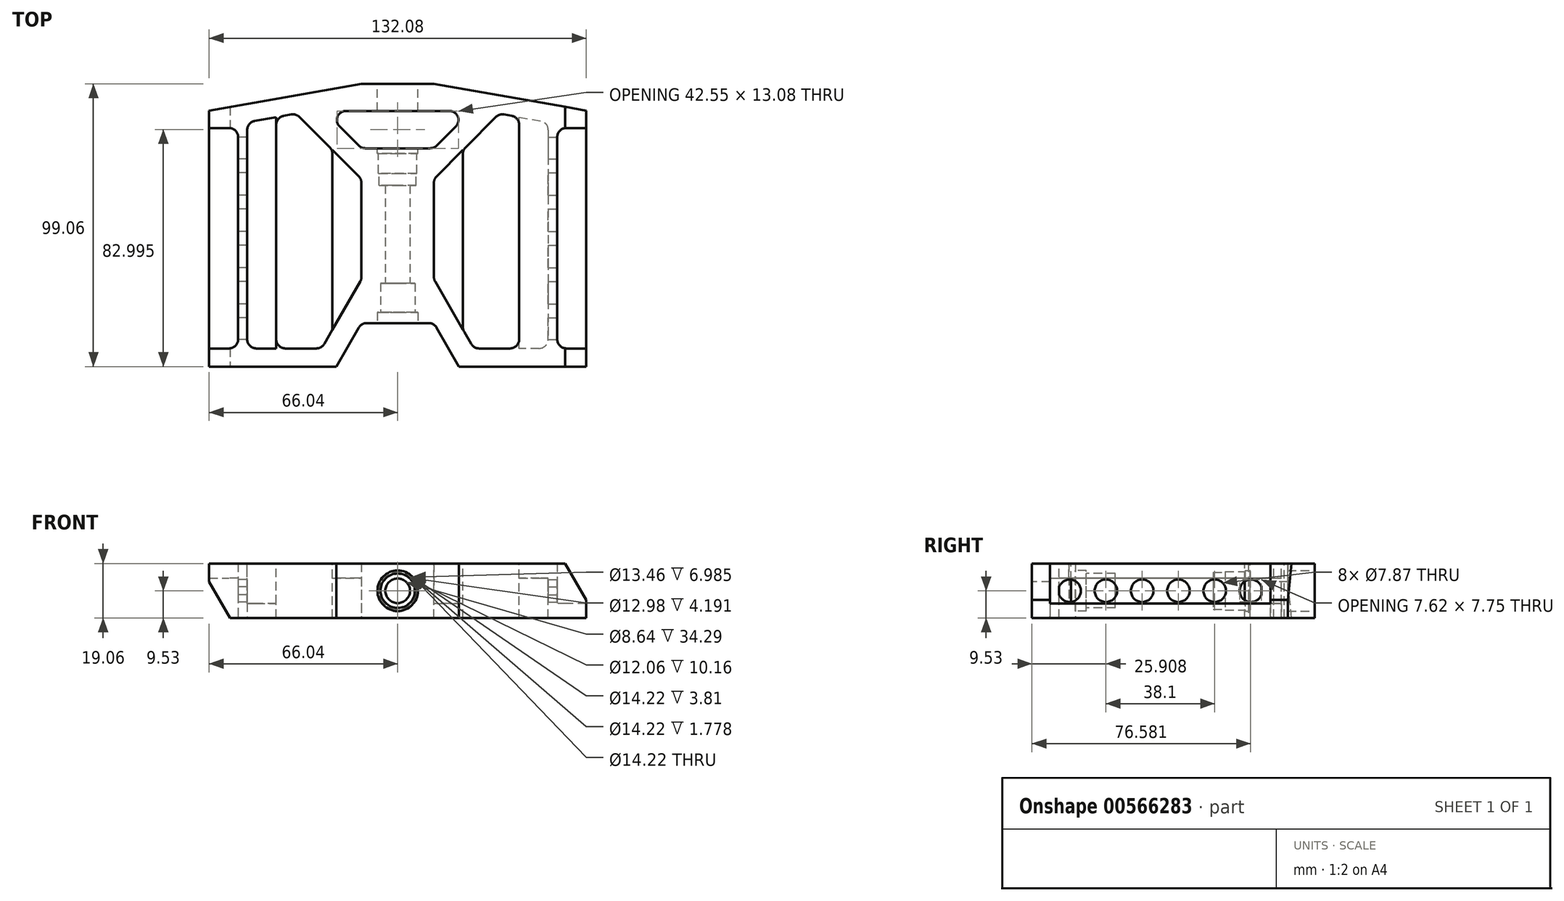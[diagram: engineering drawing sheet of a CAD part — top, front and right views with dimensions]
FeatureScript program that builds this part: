
annotation { "Feature Type Name" : "Feature", "Feature Type Description" : "" }
export const myFeature = defineFeature(function(context is Context, id is Id, definition is map)
    precondition{}
    {
        {
            var Q0;
            Q0=qCreatedBy(makeId("Top.planeOp"),FACE);
            var sketch = newSketch(context, id + "F0", { "sketchPlane" : qUnion([Q0])});
            skLineSegment(sketch, "E0", {"start": v(66.04, 89.53) * mm, "end": v(47.92, 89.53) * mm});
            skLineSegment(sketch, "E1", {"start": v(45.68, 84.11) * mm, "end": v(52.41, 77.38) * mm});
            skLineSegment(sketch, "E2", {"start": v(54.66, 76.45) * mm, "end": v(66.04, 76.45) * mm});
            skLineSegment(sketch, "E3", {"start": v(66.04, 76.45) * mm, "end": v(66.04, 89.53) * mm});
            skPoint(sketch, "E4.visualSharp", {"position": v(40.26, 89.53) * mm});
            skArc(sketch, "E4.filletArc", {"start": v(47.92, 89.53) * mm, "mid": v(45, 87.58) * mm, "end": v(45.68, 84.11) * mm});
            skPoint(sketch, "E5.visualSharp", {"position": v(53.34, 76.45) * mm});
            skArc(sketch, "E5.filletArc", {"start": v(52.41, 77.38) * mm, "mid": v(53.44, 76.7) * mm, "end": v(54.66, 76.45) * mm});
            skSolve(sketch);
        }
        {
            var Q0;
            Q0=qCreatedBy(makeId("Top.planeOp"),FACE);
            var sketch = newSketch(context, id + "F1", { "sketchPlane" : qUnion([Q0])});
            skLineSegment(sketch, "E6", {"start": v(0, 0) * mm, "end": v(0, 89.65) * mm});
            skLineSegment(sketch, "E7", {"start": v(0, 89.65) * mm, "end": v(53.34, 99.06) * mm});
            skLineSegment(sketch, "E8", {"start": v(53.34, 99.06) * mm, "end": v(66.04, 99.06) * mm});
            skLineSegment(sketch, "E9", {"start": v(66.04, 99.06) * mm, "end": v(66.04, 15.24) * mm});
            skLineSegment(sketch, "E10", {"start": v(66.04, 15.24) * mm, "end": v(55.17, 15.24) * mm});
            skLineSegment(sketch, "E11", {"start": v(52.42, 13.65) * mm, "end": v(44.54, 0) * mm});
            skLineSegment(sketch, "E12", {"start": v(44.54, 0) * mm, "end": v(0, 0) * mm});
            skPoint(sketch, "E13.visualSharp", {"position": v(53.34, 15.24) * mm});
            skArc(sketch, "E13.filletArc", {"start": v(55.17, 15.24) * mm, "mid": v(53.59, 14.81) * mm, "end": v(52.42, 13.65) * mm});
            skSolve(sketch);
        }
        {
            var Q0;
            Q0=makeQuery(id+"F1.imprint","IMPRINT",FACE,{"disambiguationData":[TD([[makeQuery(id+"F1.imprint","IMPRINT",EDGE,{"derivedFrom":sQuery(id+"F1.wireOp",EDGE,"E6")}),-1.0]])]});
            var sketch = newSketch(context, id + "F2", { "sketchPlane" : qUnion([Q0])});
            skLineSegment(sketch, "E14", {"start": v(43.18, 75.84) * mm, "end": v(43.18, 12.88) * mm});
            skLineSegment(sketch, "E15", {"start": v(43.18, 12.88) * mm, "end": v(52.91, 29.74) * mm});
            skLineSegment(sketch, "E16", {"start": v(53.34, 31.33) * mm, "end": v(53.34, 64.36) * mm});
            skLineSegment(sketch, "E17", {"start": v(52.41, 66.6) * mm, "end": v(43.18, 75.84) * mm});
            skPoint(sketch, "E18.visualSharp", {"position": v(53.34, 65.68) * mm});
            skArc(sketch, "E18.filletArc", {"start": v(53.34, 64.36) * mm, "mid": v(53.1, 65.58) * mm, "end": v(52.41, 66.6) * mm});
            skPoint(sketch, "E19.visualSharp", {"position": v(53.34, 30.48) * mm});
            skArc(sketch, "E19.filletArc", {"start": v(52.91, 29.74) * mm, "mid": v(53.23, 30.5) * mm, "end": v(53.34, 31.33) * mm});
            skSolve(sketch);
        }
        {
            var Q0;
            Q0=makeQuery(id+"F1.imprint","IMPRINT",FACE,{"disambiguationData":[TD([[makeQuery(id+"F1.imprint","IMPRINT",EDGE,{"derivedFrom":sQuery(id+"F1.wireOp",EDGE,"E6")}),-1.0]])]});
            var sketch = newSketch(context, id + "F3", { "sketchPlane" : qUnion([Q0])});
            skLineSegment(sketch, "E20", {"start": v(42.25, 76.77) * mm, "end": v(31.61, 87.4) * mm});
            skLineSegment(sketch, "E21", {"start": v(28.82, 88.29) * mm, "end": v(26.12, 87.81) * mm});
            skLineSegment(sketch, "E22", {"start": v(23.5, 84.69) * mm, "end": v(23.5, 9.52) * mm});
            skLineSegment(sketch, "E23", {"start": v(26.67, 6.35) * mm, "end": v(37.58, 6.35) * mm});
            skLineSegment(sketch, "E24", {"start": v(40.33, 7.94) * mm, "end": v(43.18, 12.88) * mm});
            skLineSegment(sketch, "E25", {"start": v(43.18, 12.88) * mm, "end": v(43.18, 74.52) * mm});
            skPoint(sketch, "E26.visualSharp", {"position": v(30.44, 88.57) * mm});
            skArc(sketch, "E26.filletArc", {"start": v(31.61, 87.4) * mm, "mid": v(30.32, 88.19) * mm, "end": v(28.82, 88.29) * mm});
            skPoint(sketch, "E27.visualSharp", {"position": v(23.5, 87.35) * mm});
            skArc(sketch, "E27.filletArc", {"start": v(26.12, 87.81) * mm, "mid": v(24.24, 86.73) * mm, "end": v(23.5, 84.69) * mm});
            skPoint(sketch, "E28.visualSharp", {"position": v(23.5, 6.35) * mm});
            skArc(sketch, "E28.filletArc", {"start": v(23.5, 9.52) * mm, "mid": v(24.42, 7.28) * mm, "end": v(26.67, 6.35) * mm});
            skPoint(sketch, "E29.visualSharp", {"position": v(39.4, 6.35) * mm});
            skArc(sketch, "E29.filletArc", {"start": v(37.58, 6.35) * mm, "mid": v(39.16, 6.78) * mm, "end": v(40.33, 7.94) * mm});
            skPoint(sketch, "E30.visualSharp", {"position": v(43.18, 75.84) * mm});
            skArc(sketch, "E30.filletArc", {"start": v(43.18, 74.52) * mm, "mid": v(42.94, 75.74) * mm, "end": v(42.25, 76.77) * mm});
            skCircle(sketch, "E31", {"center": v(40, 13.73) * mm, "radius": 3.18 * mm});
            skSolve(sketch);
        }
        {
            var Q0;
            Q0=makeQuery(id+"F1.imprint","IMPRINT",FACE,{"disambiguationData":[TD([[makeQuery(id+"F1.imprint","IMPRINT",EDGE,{"derivedFrom":sQuery(id+"F1.wireOp",EDGE,"E6")}),-1.0]])]});
            var sketch = newSketch(context, id + "F4", { "sketchPlane" : qUnion([Q0])});
            skLineSegment(sketch, "E32", {"start": v(23.5, 87.35) * mm, "end": v(15.96, 86.02) * mm});
            skLineSegment(sketch, "E33", {"start": v(13.33, 82.9) * mm, "end": v(13.33, 9.52) * mm});
            skLineSegment(sketch, "E34", {"start": v(16.5, 6.35) * mm, "end": v(23.5, 6.35) * mm});
            skLineSegment(sketch, "E35", {"start": v(23.5, 6.35) * mm, "end": v(23.5, 87.35) * mm});
            skPoint(sketch, "E36.visualSharp", {"position": v(13.33, 85.56) * mm});
            skArc(sketch, "E36.filletArc", {"start": v(15.96, 86.02) * mm, "mid": v(14.08, 84.93) * mm, "end": v(13.33, 82.9) * mm});
            skPoint(sketch, "E37.visualSharp", {"position": v(13.33, 6.35) * mm});
            skArc(sketch, "E37.filletArc", {"start": v(13.34, 9.52) * mm, "mid": v(14.26, 7.28) * mm, "end": v(16.5, 6.35) * mm});
            skLineSegment(sketch, "E38", {"start": v(23.5, 6.35) * mm, "end": v(26.7, 6.35) * mm});
            skLineSegment(sketch, "E39", {"start": v(23.5, 87.35) * mm, "end": v(26.43, 87.35) * mm});
            skSolve(sketch);
        }
        {
            var Q0;
            Q0=makeQuery(id+"F1.imprint","IMPRINT",FACE,{"disambiguationData":[TD([[makeQuery(id+"F1.imprint","IMPRINT",EDGE,{"derivedFrom":sQuery(id+"F1.wireOp",EDGE,"E6")}),-1.0]])]});
            var sketch = newSketch(context, id + "F5", { "sketchPlane" : qUnion([Q0])});
            skLineSegment(sketch, "E40", {"start": v(0, 83.57) * mm, "end": v(6.99, 83.57) * mm});
            skLineSegment(sketch, "E41", {"start": v(10.16, 80.4) * mm, "end": v(10.16, 9.52) * mm});
            skLineSegment(sketch, "E42", {"start": v(6.99, 6.35) * mm, "end": v(0, 6.35) * mm});
            skLineSegment(sketch, "E43", {"start": v(0, 6.35) * mm, "end": v(0, 83.57) * mm});
            skPoint(sketch, "E44.visualSharp", {"position": v(10.16, 83.57) * mm});
            skArc(sketch, "E44.filletArc", {"start": v(10.16, 80.4) * mm, "mid": v(9.23, 82.64) * mm, "end": v(6.99, 83.57) * mm});
            skPoint(sketch, "E45.visualSharp", {"position": v(10.16, 6.35) * mm});
            skArc(sketch, "E45.filletArc", {"start": v(6.99, 6.35) * mm, "mid": v(9.23, 7.28) * mm, "end": v(10.16, 9.52) * mm});
            skSolve(sketch);
        }
        {
            var Q0;
            Q0 = qSketchRegion(id + "F1", true);
            var Q1;
            Q1 = qSketchRegion(id + "F2", true);
            var Q2;
            Q2 = qSketchRegion(id + "F4", true);
            var Q3;
            Q3 = qSketchRegion(id + "F5", true);
            var Q4;
            Q4 = qSketchRegion(id + "F0", true);
            var Q5;
            Q5 = qSketchRegion(id + "F3", true);
            extrude(context, id + "F6", {"entities" : qUnion([Q0, Q1, Q2, Q3, Q4, Q5]), "endBound" : BoundingType.SYMMETRIC, "depth" : 19.05 * mm, "offsetDistance" : 25.4 * mm});
        }
        {
            var Q0;
            Q0=makeQuery(id+"F6.opExtrude","CAP_FACE",FACE,{"disambiguationData":[OSD([sQuery(id+"F0.wireOp",EDGE,"E0"),sQuery(id+"F0.wireOp",EDGE,"E1"),sQuery(id+"F0.wireOp",EDGE,"E2"),sQuery(id+"F0.wireOp",EDGE,"E3"),sQuery(id+"F0.wireOp",EDGE,"E4.filletArc"),sQuery(id+"F0.wireOp",EDGE,"E5.filletArc")])],"isStart":false});
            extrude(context, id + "F7", {"entities" : qUnion([Q0]), "operationType" : NewBodyOperationType.REMOVE, "endBound" : BoundingType.THROUGH_ALL, "oppositeDirection" : true, "depth" : 25.4 * mm, "offsetDistance" : 25.4 * mm});
        }
        {
            var Q0;
            Q0=makeQuery(id+"F6.opExtrude","CAP_FACE",FACE,{"disambiguationData":[OSD([sQuery(id+"F3.wireOp",EDGE,"E20"),sQuery(id+"F3.wireOp",EDGE,"E21"),sQuery(id+"F3.wireOp",EDGE,"E22"),sQuery(id+"F3.wireOp",EDGE,"E23"),sQuery(id+"F3.wireOp",EDGE,"E24"),sQuery(id+"F3.wireOp",EDGE,"E25"),sQuery(id+"F3.wireOp",EDGE,"E26.filletArc"),sQuery(id+"F3.wireOp",EDGE,"E27.filletArc"),sQuery(id+"F3.wireOp",EDGE,"E28.filletArc"),sQuery(id+"F3.wireOp",EDGE,"E29.filletArc"),sQuery(id+"F3.wireOp",EDGE,"E30.filletArc")])],"isStart":false});
            extrude(context, id + "F8", {"entities" : qUnion([Q0]), "operationType" : NewBodyOperationType.REMOVE, "endBound" : BoundingType.THROUGH_ALL, "oppositeDirection" : true, "depth" : 25.4 * mm, "offsetDistance" : 25.4 * mm});
        }
        {
            var Q0;
            Q0=makeQuery(id+"F6.opExtrude","CAP_FACE",FACE,{"disambiguationData":[OSD([sQuery(id+"F4.wireOp",EDGE,"E32"),sQuery(id+"F4.wireOp",EDGE,"E33"),sQuery(id+"F4.wireOp",EDGE,"E34"),sQuery(id+"F4.wireOp",EDGE,"E35"),sQuery(id+"F4.wireOp",EDGE,"E36.filletArc"),sQuery(id+"F4.wireOp",EDGE,"E37.filletArc")])],"isStart":false});
            extrude(context, id + "F9", {"entities" : qUnion([Q0]), "operationType" : NewBodyOperationType.REMOVE, "oppositeDirection" : true, "depth" : 13.97 * mm, "offsetDistance" : 25.4 * mm});
        }
        {
            var Q0;
            Q0=makeQuery(id+"F6.opExtrude","CAP_FACE",FACE,{"disambiguationData":[OSD([sQuery(id+"F5.wireOp",EDGE,"E40"),sQuery(id+"F5.wireOp",EDGE,"E41"),sQuery(id+"F5.wireOp",EDGE,"E42"),sQuery(id+"F5.wireOp",EDGE,"E43"),sQuery(id+"F5.wireOp",EDGE,"E44.filletArc"),sQuery(id+"F5.wireOp",EDGE,"E45.filletArc")])],"isStart":true});
            extrude(context, id + "F10", {"entities" : qUnion([Q0]), "operationType" : NewBodyOperationType.REMOVE, "oppositeDirection" : true, "depth" : 13.97 * mm, "offsetDistance" : 25.4 * mm});
        }
        {
            var Q0;
            Q0=makeQuery(id+"F6.opExtrude","CAP_FACE",FACE,{"disambiguationData":[OSD([sQuery(id+"F2.wireOp",EDGE,"E14"),sQuery(id+"F2.wireOp",EDGE,"E15"),sQuery(id+"F2.wireOp",EDGE,"E16"),sQuery(id+"F2.wireOp",EDGE,"E17"),sQuery(id+"F2.wireOp",EDGE,"E18.filletArc"),sQuery(id+"F2.wireOp",EDGE,"E19.filletArc")])],"isStart":true});
            extrude(context, id + "F11", {"entities" : qUnion([Q0]), "operationType" : NewBodyOperationType.REMOVE, "oppositeDirection" : true, "depth" : 13.97 * mm, "offsetDistance" : 25.4 * mm});
        }
        {
            var Q0;
            Q0=qCreatedBy(makeId("Top.planeOp"),FACE);
            var sketch = newSketch(context, id + "F12", { "sketchPlane" : qUnion([Q0])});
            skLineSegment(sketch, "E46", {"start": v(66.04, 15.24) * mm, "end": v(66.04, 99.06) * mm});
            skLineSegment(sketch, "E47", {"start": v(66.04, 99.06) * mm, "end": v(78.74, 99.06) * mm});
            skLineSegment(sketch, "E48", {"start": v(78.74, 99.06) * mm, "end": v(132.08, 89.65) * mm});
            skLineSegment(sketch, "E49", {"start": v(132.08, 89.65) * mm, "end": v(132.08, 0) * mm});
            skLineSegment(sketch, "E50", {"start": v(132.08, 0) * mm, "end": v(87.54, 0) * mm});
            skLineSegment(sketch, "E51", {"start": v(87.54, 0) * mm, "end": v(79.66, 13.65) * mm});
            skLineSegment(sketch, "E52", {"start": v(76.9, 15.24) * mm, "end": v(66.04, 15.24) * mm});
            skPoint(sketch, "E53.visualSharp", {"position": v(78.74, 15.24) * mm});
            skArc(sketch, "E53.filletArc", {"start": v(79.66, 13.65) * mm, "mid": v(78.5, 14.81) * mm, "end": v(76.9, 15.24) * mm});
            skSolve(sketch);
        }
        {
            var Q0;
            Q0=makeQuery(id+"F12.imprint","IMPRINT",FACE,{"disambiguationData":[TD([[makeQuery(id+"F12.imprint","IMPRINT",EDGE,{"derivedFrom":sQuery(id+"F12.wireOp",EDGE,"E46")}),-1.0]])]});
            var sketch = newSketch(context, id + "F13", { "sketchPlane" : qUnion([Q0])});
            skLineSegment(sketch, "E54", {"start": v(66.04, 89.53) * mm, "end": v(84.16, 89.53) * mm});
            skLineSegment(sketch, "E55", {"start": v(86.4, 84.11) * mm, "end": v(79.67, 77.38) * mm});
            skLineSegment(sketch, "E56", {"start": v(77.42, 76.45) * mm, "end": v(66.04, 76.45) * mm});
            skLineSegment(sketch, "E57", {"start": v(66.04, 76.45) * mm, "end": v(66.04, 89.53) * mm});
            skPoint(sketch, "E58.visualSharp", {"position": v(91.82, 89.53) * mm});
            skArc(sketch, "E58.filletArc", {"start": v(86.4, 84.11) * mm, "mid": v(87.09, 87.58) * mm, "end": v(84.16, 89.54) * mm});
            skPoint(sketch, "E59.visualSharp", {"position": v(78.74, 76.45) * mm});
            skArc(sketch, "E59.filletArc", {"start": v(77.42, 76.45) * mm, "mid": v(78.64, 76.7) * mm, "end": v(79.67, 77.38) * mm});
            skSolve(sketch);
        }
        {
            var Q0;
            Q0=makeQuery(id+"F12.imprint","IMPRINT",FACE,{"disambiguationData":[TD([[makeQuery(id+"F12.imprint","IMPRINT",EDGE,{"derivedFrom":sQuery(id+"F12.wireOp",EDGE,"E46")}),-1.0]])]});
            var sketch = newSketch(context, id + "F14", { "sketchPlane" : qUnion([Q0])});
            skLineSegment(sketch, "E60", {"start": v(88.9, 75.84) * mm, "end": v(88.9, 12.88) * mm});
            skLineSegment(sketch, "E61", {"start": v(88.9, 12.88) * mm, "end": v(79.17, 29.74) * mm});
            skLineSegment(sketch, "E62", {"start": v(78.74, 31.33) * mm, "end": v(78.74, 64.36) * mm});
            skLineSegment(sketch, "E63", {"start": v(79.67, 66.6) * mm, "end": v(88.9, 75.84) * mm});
            skPoint(sketch, "E64.visualSharp", {"position": v(78.74, 65.68) * mm});
            skArc(sketch, "E64.filletArc", {"start": v(79.67, 66.6) * mm, "mid": v(78.98, 65.58) * mm, "end": v(78.74, 64.36) * mm});
            skPoint(sketch, "E65.visualSharp", {"position": v(78.74, 30.48) * mm});
            skArc(sketch, "E65.filletArc", {"start": v(78.74, 31.33) * mm, "mid": v(78.85, 30.5) * mm, "end": v(79.17, 29.74) * mm});
            skSolve(sketch);
        }
        {
            var Q0;
            Q0=makeQuery(id+"F12.imprint","IMPRINT",FACE,{"disambiguationData":[TD([[makeQuery(id+"F12.imprint","IMPRINT",EDGE,{"derivedFrom":sQuery(id+"F12.wireOp",EDGE,"E46")}),-1.0]])]});
            var sketch = newSketch(context, id + "F15", { "sketchPlane" : qUnion([Q0])});
            skLineSegment(sketch, "E66", {"start": v(89.83, 76.77) * mm, "end": v(100.47, 87.4) * mm});
            skLineSegment(sketch, "E67", {"start": v(103.26, 88.29) * mm, "end": v(105.96, 87.81) * mm});
            skLineSegment(sketch, "E68", {"start": v(108.58, 84.69) * mm, "end": v(108.58, 9.53) * mm});
            skLineSegment(sketch, "E69", {"start": v(105.4, 6.35) * mm, "end": v(94.5, 6.35) * mm});
            skLineSegment(sketch, "E70", {"start": v(91.75, 7.94) * mm, "end": v(89.33, 12.15) * mm});
            skLineSegment(sketch, "E71", {"start": v(88.9, 13.73) * mm, "end": v(88.9, 74.52) * mm});
            skPoint(sketch, "E72.visualSharp", {"position": v(101.64, 88.57) * mm});
            skArc(sketch, "E72.filletArc", {"start": v(103.26, 88.29) * mm, "mid": v(101.76, 88.19) * mm, "end": v(100.47, 87.4) * mm});
            skPoint(sketch, "E73.visualSharp", {"position": v(108.59, 87.35) * mm});
            skArc(sketch, "E73.filletArc", {"start": v(108.59, 84.69) * mm, "mid": v(107.84, 86.73) * mm, "end": v(105.96, 87.81) * mm});
            skPoint(sketch, "E74.visualSharp", {"position": v(108.59, 6.35) * mm});
            skArc(sketch, "E74.filletArc", {"start": v(105.4, 6.35) * mm, "mid": v(107.66, 7.28) * mm, "end": v(108.59, 9.53) * mm});
            skPoint(sketch, "E75.visualSharp", {"position": v(92.67, 6.35) * mm});
            skArc(sketch, "E75.filletArc", {"start": v(91.75, 7.94) * mm, "mid": v(92.92, 6.78) * mm, "end": v(94.5, 6.35) * mm});
            skPoint(sketch, "E76.visualSharp", {"position": v(88.9, 75.84) * mm});
            skArc(sketch, "E76.filletArc", {"start": v(89.83, 76.77) * mm, "mid": v(89.14, 75.74) * mm, "end": v(88.9, 74.52) * mm});
            skPoint(sketch, "E77.visualSharp", {"position": v(88.9, 12.88) * mm});
            skArc(sketch, "E77.filletArc", {"start": v(88.9, 13.73) * mm, "mid": v(89, 12.91) * mm, "end": v(89.33, 12.15) * mm});
            skSolve(sketch);
        }
        {
            var Q0;
            Q0=makeQuery(id+"F12.imprint","IMPRINT",FACE,{"disambiguationData":[TD([[makeQuery(id+"F12.imprint","IMPRINT",EDGE,{"derivedFrom":sQuery(id+"F12.wireOp",EDGE,"E46")}),-1.0]])]});
            var sketch = newSketch(context, id + "F16", { "sketchPlane" : qUnion([Q0])});
            skLineSegment(sketch, "E78", {"start": v(108.59, 87.35) * mm, "end": v(116.12, 86.02) * mm});
            skLineSegment(sketch, "E79", {"start": v(118.75, 82.9) * mm, "end": v(118.75, 9.53) * mm});
            skLineSegment(sketch, "E80", {"start": v(115.57, 6.35) * mm, "end": v(108.59, 6.35) * mm});
            skLineSegment(sketch, "E81", {"start": v(108.59, 6.35) * mm, "end": v(108.59, 87.35) * mm});
            skPoint(sketch, "E82.visualSharp", {"position": v(118.75, 85.56) * mm});
            skArc(sketch, "E82.filletArc", {"start": v(118.75, 82.9) * mm, "mid": v(118, 84.93) * mm, "end": v(116.12, 86.02) * mm});
            skPoint(sketch, "E83.visualSharp", {"position": v(118.75, 6.35) * mm});
            skArc(sketch, "E83.filletArc", {"start": v(115.57, 6.35) * mm, "mid": v(117.82, 7.28) * mm, "end": v(118.75, 9.53) * mm});
            skSolve(sketch);
        }
        {
            var Q0;
            Q0=makeQuery(id+"F12.imprint","IMPRINT",FACE,{"disambiguationData":[TD([[makeQuery(id+"F12.imprint","IMPRINT",EDGE,{"derivedFrom":sQuery(id+"F12.wireOp",EDGE,"E46")}),-1.0]])]});
            var sketch = newSketch(context, id + "F17", { "sketchPlane" : qUnion([Q0])});
            skLineSegment(sketch, "E84", {"start": v(132.08, 83.57) * mm, "end": v(125.1, 83.57) * mm});
            skLineSegment(sketch, "E85", {"start": v(121.92, 80.4) * mm, "end": v(121.92, 9.53) * mm});
            skLineSegment(sketch, "E86", {"start": v(125.1, 6.35) * mm, "end": v(132.08, 6.35) * mm});
            skLineSegment(sketch, "E87", {"start": v(132.08, 6.35) * mm, "end": v(132.08, 83.57) * mm});
            skPoint(sketch, "E88.visualSharp", {"position": v(121.92, 83.57) * mm});
            skArc(sketch, "E88.filletArc", {"start": v(125.1, 83.57) * mm, "mid": v(122.85, 82.64) * mm, "end": v(121.92, 80.4) * mm});
            skPoint(sketch, "E89.visualSharp", {"position": v(121.92, 6.35) * mm});
            skArc(sketch, "E89.filletArc", {"start": v(121.92, 9.53) * mm, "mid": v(122.85, 7.28) * mm, "end": v(125.1, 6.35) * mm});
            skSolve(sketch);
        }
        {
            var Q0;
            Q0=makeQuery(id+"F12.imprint","IMPRINT",FACE,{"disambiguationData":[TD([[makeQuery(id+"F12.imprint","IMPRINT",EDGE,{"derivedFrom":sQuery(id+"F12.wireOp",EDGE,"E46")}),-1.0]])]});
            extrude(context, id + "F18", {"entities" : qUnion([Q0]), "operationType" : NewBodyOperationType.ADD, "endBound" : BoundingType.SYMMETRIC, "oppositeDirection" : true, "depth" : 19.05 * mm, "offsetDistance" : 25.4 * mm});
        }
        {
            var Q0;
            Q0 = qSketchRegion(id + "F13", true);
            extrude(context, id + "F19", {"entities" : qUnion([Q0]), "operationType" : NewBodyOperationType.REMOVE, "endBound" : BoundingType.SYMMETRIC, "depth" : 19.05 * mm, "offsetDistance" : 25.4 * mm});
        }
        {
            var Q0;
            Q0 = qSketchRegion(id + "F15", true);
            extrude(context, id + "F20", {"entities" : qUnion([Q0]), "operationType" : NewBodyOperationType.REMOVE, "endBound" : BoundingType.SYMMETRIC, "oppositeDirection" : true, "depth" : 19.05 * mm, "offsetDistance" : 25.4 * mm});
        }
        {
            var Q0;
            Q0 = qSketchRegion(id + "F14", true);
            extrude(context, id + "F21", {"entities" : qUnion([Q0]), "operationType" : NewBodyOperationType.REMOVE, "depth" : 9.52 * mm, "offsetDistance" : 25.4 * mm, "hasSecondDirection" : true, "secondDirectionOppositeDirection" : true, "secondDirectionDepth" : 4.44 * mm});
        }
        {
            var Q0;
            Q0 = qSketchRegion(id + "F16", true);
            extrude(context, id + "F22", {"entities" : qUnion([Q0]), "operationType" : NewBodyOperationType.REMOVE, "oppositeDirection" : true, "depth" : 9.52 * mm, "offsetDistance" : 25.4 * mm, "hasSecondDirection" : true, "secondDirectionOppositeDirection" : false, "secondDirectionDepth" : 4.44 * mm});
        }
        {
            var Q0;
            Q0 = qSketchRegion(id + "F17", true);
            extrude(context, id + "F23", {"entities" : qUnion([Q0]), "operationType" : NewBodyOperationType.REMOVE, "depth" : 9.52 * mm, "offsetDistance" : 25.4 * mm, "hasSecondDirection" : true, "secondDirectionOppositeDirection" : true, "secondDirectionDepth" : 4.44 * mm});
        }
        {
            var Q0;
            Q0=makeQuery(id+"F10.boolean.opBoolean","COPY",FACE,{"derivedFrom":makeQuery(id+"F10.opExtrude","SWEPT_FACE",FACE,{"disambiguationData":[OSD([sQuery(id+"F5.wireOp",EDGE,"E41")])]})});
            var sketch = newSketch(context, id + "F24", { "sketchPlane" : qUnion([Q0])});
            skCircle(sketch, "E90", {"center": v(-13.2, 0) * mm, "radius": 3.94 * mm});
            skCircle(sketch, "E91.1.0.0", {"center": v(-25.9, 0) * mm, "radius": 3.94 * mm});
            skCircle(sketch, "E91.2.0.0", {"center": v(-38.6, 0) * mm, "radius": 3.94 * mm});
            skCircle(sketch, "E91.3.0.0", {"center": v(-51.3, 0) * mm, "radius": 3.94 * mm});
            skCircle(sketch, "E91.4.0.0", {"center": v(-64, 0) * mm, "radius": 3.94 * mm});
            skCircle(sketch, "E91.5.0.0", {"center": v(-76.7, 0) * mm, "radius": 3.94 * mm});
            skLineSegment(sketch, "E91.direction1", {"start": v(-13.2, 0) * mm, "end": v(-25.9, 0) * mm, "construction": true});
            skSolve(sketch);
        }
        {
            var Q0;
            {var subQ0=sQuery(id+"F24.wireOp",EDGE,"E91.5.0.0");var subQ1=makeQuery(id+"F10.boolean.opBoolean","COPY",EDGE,{"derivedFrom":makeQuery(id+"F10.opExtrude","SWEPT_EDGE",EDGE,{"disambiguationData":[OSD([sQuery(id+"F5.wireOp",EDGE,"E41"),sQuery(id+"F5.wireOp",EDGE,"E44.filletArc")])]})});var subQ2=makeQuery(id+"F24.imprint","INTERSECT",VERTEX,{"disambiguationData":[OD(0.0)],"derivedFrom":[subQ1,subQ0]});Q0=makeQuery(id+"F24.imprint","IMPRINT",FACE,{"disambiguationData":[TD([[makeQuery(id+"F24.imprint","IMPRINT",EDGE,{"disambiguationData":[TD([[subQ2,-1.0]])],"derivedFrom":subQ0}),1.0]])]});}
            var Q1;
            Q1=makeQuery(id+"F24.imprint","IMPRINT",FACE,{"disambiguationData":[TD([[makeQuery(id+"F24.imprint","IMPRINT",EDGE,{"derivedFrom":sQuery(id+"F24.wireOp",EDGE,"E91.4.0.0")}),1.0]])]});
            var Q2;
            Q2=makeQuery(id+"F24.imprint","IMPRINT",FACE,{"disambiguationData":[TD([[makeQuery(id+"F24.imprint","IMPRINT",EDGE,{"derivedFrom":sQuery(id+"F24.wireOp",EDGE,"E91.3.0.0")}),1.0]])]});
            var Q3;
            Q3=makeQuery(id+"F24.imprint","IMPRINT",FACE,{"disambiguationData":[TD([[makeQuery(id+"F24.imprint","IMPRINT",EDGE,{"derivedFrom":sQuery(id+"F24.wireOp",EDGE,"E91.2.0.0")}),1.0]])]});
            var Q4;
            Q4=makeQuery(id+"F24.imprint","IMPRINT",FACE,{"disambiguationData":[TD([[makeQuery(id+"F24.imprint","IMPRINT",EDGE,{"derivedFrom":sQuery(id+"F24.wireOp",EDGE,"E91.1.0.0")}),1.0]])]});
            var Q5;
            {var subQ0=sQuery(id+"F24.wireOp",EDGE,"E90");var subQ1=makeQuery(id+"F10.boolean.opBoolean","COPY",EDGE,{"derivedFrom":makeQuery(id+"F10.opExtrude","SWEPT_EDGE",EDGE,{"disambiguationData":[OSD([sQuery(id+"F5.wireOp",EDGE,"E41"),sQuery(id+"F5.wireOp",EDGE,"E45.filletArc")])]})});var subQ2=makeQuery(id+"F24.imprint","INTERSECT",VERTEX,{"disambiguationData":[OD(0.0)],"derivedFrom":[subQ1,subQ0]});Q5=makeQuery(id+"F24.imprint","IMPRINT",FACE,{"disambiguationData":[TD([[makeQuery(id+"F24.imprint","IMPRINT",EDGE,{"disambiguationData":[TD([[subQ2,1.0]])],"derivedFrom":subQ0}),1.0]])]});}
            extrude(context, id + "F25", {"entities" : qUnion([Q0, Q1, Q2, Q3, Q4, Q5]), "operationType" : NewBodyOperationType.REMOVE, "oppositeDirection" : true, "depth" : 3.17 * mm, "offsetDistance" : 25.4 * mm});
        }
        {
            var Q0;
            Q0=makeQuery(id+"F23.boolean.opBoolean","COPY",FACE,{"derivedFrom":makeQuery(id+"F23.opExtrude","SWEPT_FACE",FACE,{"disambiguationData":[OSD([sQuery(id+"F17.wireOp",EDGE,"E85")])]})});
            var sketch = newSketch(context, id + "F26", { "sketchPlane" : qUnion([Q0])});
            skCircle(sketch, "E92", {"center": v(13.2, 0) * mm, "radius": 3.94 * mm});
            skCircle(sketch, "E93.1.0.0", {"center": v(25.9, 0) * mm, "radius": 3.94 * mm});
            skCircle(sketch, "E93.2.0.0", {"center": v(38.6, 0) * mm, "radius": 3.94 * mm});
            skCircle(sketch, "E93.3.0.0", {"center": v(51.3, 0) * mm, "radius": 3.94 * mm});
            skCircle(sketch, "E93.4.0.0", {"center": v(64, 0) * mm, "radius": 3.94 * mm});
            skCircle(sketch, "E93.5.0.0", {"center": v(76.7, 0) * mm, "radius": 3.94 * mm});
            skLineSegment(sketch, "E93.direction1", {"start": v(13.2, 0) * mm, "end": v(25.9, 0) * mm, "construction": true});
            skSolve(sketch);
        }
        {
            var Q0;
            {var subQ0=sQuery(id+"F26.wireOp",EDGE,"E92");var subQ1=makeQuery(id+"F23.boolean.opBoolean","COPY",EDGE,{"derivedFrom":makeQuery(id+"F23.opExtrude","SWEPT_EDGE",EDGE,{"disambiguationData":[OSD([sQuery(id+"F17.wireOp",EDGE,"E85"),sQuery(id+"F17.wireOp",EDGE,"E89.filletArc")])]})});var subQ2=makeQuery(id+"F26.imprint","INTERSECT",VERTEX,{"disambiguationData":[OD(0.0)],"derivedFrom":[subQ1,subQ0]});Q0=makeQuery(id+"F26.imprint","IMPRINT",FACE,{"disambiguationData":[TD([[makeQuery(id+"F26.imprint","IMPRINT",EDGE,{"disambiguationData":[TD([[subQ2,-1.0]])],"derivedFrom":subQ0}),1.0]])]});}
            var Q1;
            Q1=makeQuery(id+"F26.imprint","IMPRINT",FACE,{"disambiguationData":[TD([[makeQuery(id+"F26.imprint","IMPRINT",EDGE,{"derivedFrom":sQuery(id+"F26.wireOp",EDGE,"E93.1.0.0")}),1.0]])]});
            var Q2;
            Q2=makeQuery(id+"F26.imprint","IMPRINT",FACE,{"disambiguationData":[TD([[makeQuery(id+"F26.imprint","IMPRINT",EDGE,{"derivedFrom":sQuery(id+"F26.wireOp",EDGE,"E93.2.0.0")}),1.0]])]});
            var Q3;
            Q3=makeQuery(id+"F26.imprint","IMPRINT",FACE,{"disambiguationData":[TD([[makeQuery(id+"F26.imprint","IMPRINT",EDGE,{"derivedFrom":sQuery(id+"F26.wireOp",EDGE,"E93.3.0.0")}),1.0]])]});
            var Q4;
            Q4=makeQuery(id+"F26.imprint","IMPRINT",FACE,{"disambiguationData":[TD([[makeQuery(id+"F26.imprint","IMPRINT",EDGE,{"derivedFrom":sQuery(id+"F26.wireOp",EDGE,"E93.4.0.0")}),1.0]])]});
            var Q5;
            {var subQ0=sQuery(id+"F26.wireOp",EDGE,"E93.5.0.0");var subQ1=makeQuery(id+"F23.boolean.opBoolean","COPY",EDGE,{"derivedFrom":makeQuery(id+"F23.opExtrude","SWEPT_EDGE",EDGE,{"disambiguationData":[OSD([sQuery(id+"F17.wireOp",EDGE,"E85"),sQuery(id+"F17.wireOp",EDGE,"E88.filletArc")])]})});var subQ2=makeQuery(id+"F26.imprint","INTERSECT",VERTEX,{"disambiguationData":[OD(0.0)],"derivedFrom":[subQ1,subQ0]});Q5=makeQuery(id+"F26.imprint","IMPRINT",FACE,{"disambiguationData":[TD([[makeQuery(id+"F26.imprint","IMPRINT",EDGE,{"disambiguationData":[TD([[subQ2,1.0]])],"derivedFrom":subQ0}),1.0]])]});}
            extrude(context, id + "F27", {"entities" : qUnion([Q0, Q1, Q2, Q3, Q4, Q5]), "operationType" : NewBodyOperationType.REMOVE, "oppositeDirection" : true, "depth" : 3.17 * mm, "offsetDistance" : 25.4 * mm});
        }
        {
            var Q0;
            Q0=makeQuery(id+"F18.boolean.opBoolean","MERGE",FACE,{"derivedFrom":[makeQuery(id+"F6.opExtrude","SWEPT_FACE",FACE,{"disambiguationData":[OSD([sQuery(id+"F1.wireOp",EDGE,"E10")])]}),makeQuery(id+"F18.opExtrude","SWEPT_FACE",FACE,{"disambiguationData":[OSD([sQuery(id+"F12.wireOp",EDGE,"E52")])]})]});
            var sketch = newSketch(context, id + "F28", { "sketchPlane" : qUnion([Q0])});
            skCircle(sketch, "E94", {"center": v(66.04, 0) * mm, "radius": 4.32 * mm});
            skPoint(sketch, "E94.centerSnap0", {"position": v(66.04, 9.53) * mm});
            skSolve(sketch);
        }
        {
            var Q0;
            Q0 = qSketchRegion(id + "F28", true);
            extrude(context, id + "F29", {"entities" : qUnion([Q0]), "operationType" : NewBodyOperationType.REMOVE, "endBound" : BoundingType.THROUGH_ALL, "oppositeDirection" : true, "depth" : 25.4 * mm, "offsetDistance" : 25.4 * mm});
        }
        {
            var Q0;
            Q0=makeQuery(id+"F18.boolean.opBoolean","MERGE",FACE,{"derivedFrom":[makeQuery(id+"F6.opExtrude","SWEPT_FACE",FACE,{"disambiguationData":[OSD([sQuery(id+"F1.wireOp",EDGE,"E10")])]}),makeQuery(id+"F18.opExtrude","SWEPT_FACE",FACE,{"disambiguationData":[OSD([sQuery(id+"F12.wireOp",EDGE,"E52")])]})]});
            var sketch = newSketch(context, id + "F30", { "sketchPlane" : qUnion([Q0])});
            skCircle(sketch, "E95", {"center": v(66.04, 0) * mm, "radius": 6.03 * mm});
            skSolve(sketch);
        }
        {
            var Q0;
            Q0 = qSketchRegion(id + "F30", true);
            extrude(context, id + "F31", {"entities" : qUnion([Q0]), "operationType" : NewBodyOperationType.REMOVE, "oppositeDirection" : true, "depth" : 13.97 * mm, "offsetDistance" : 25.4 * mm});
        }
        {
            var Q0;
            Q0=makeQuery(id+"F18.boolean.opBoolean","MERGE",FACE,{"derivedFrom":[makeQuery(id+"F6.opExtrude","SWEPT_FACE",FACE,{"disambiguationData":[OSD([sQuery(id+"F1.wireOp",EDGE,"E10")])]}),makeQuery(id+"F18.opExtrude","SWEPT_FACE",FACE,{"disambiguationData":[OSD([sQuery(id+"F12.wireOp",EDGE,"E52")])]})]});
            var sketch = newSketch(context, id + "F32", { "sketchPlane" : qUnion([Q0])});
            skCircle(sketch, "E96", {"center": v(66.04, 0) * mm, "radius": 7.11 * mm});
            skSolve(sketch);
        }
        {
            var Q0;
            Q0 = qSketchRegion(id + "F32", true);
            extrude(context, id + "F33", {"entities" : qUnion([Q0]), "operationType" : NewBodyOperationType.REMOVE, "oppositeDirection" : true, "depth" : 3.8 * mm, "offsetDistance" : 25.4 * mm});
        }
        {
            var Q0;
            Q0=makeQuery(id+"F18.boolean.opBoolean","MERGE",FACE,{"derivedFrom":[makeQuery(id+"F6.opExtrude","SWEPT_FACE",FACE,{"disambiguationData":[OSD([sQuery(id+"F1.wireOp",EDGE,"E8")])]}),makeQuery(id+"F18.opExtrude","SWEPT_FACE",FACE,{"disambiguationData":[OSD([sQuery(id+"F12.wireOp",EDGE,"E47")])]})]});
            var sketch = newSketch(context, id + "F34", { "sketchPlane" : qUnion([Q0])});
            skCircle(sketch, "E97", {"center": v(-66.04, 0) * mm, "radius": 6.49 * mm});
            skSolve(sketch);
        }
        {
            var Q0;
            Q0=makeQuery(id+"F34.imprint","IMPRINT",FACE,{"disambiguationData":[TD([[makeQuery(id+"F34.imprint","IMPRINT",EDGE,{"derivedFrom":sQuery(id+"F34.wireOp",EDGE,"E97")}),1.0]])]});
            extrude(context, id + "F35", {"entities" : qUnion([Q0]), "operationType" : NewBodyOperationType.REMOVE, "oppositeDirection" : true, "depth" : 35.56 * mm, "offsetDistance" : 25.4 * mm});
        }
        {
            var Q0;
            Q0=makeQuery(id+"F18.boolean.opBoolean","MERGE",FACE,{"derivedFrom":[makeQuery(id+"F6.opExtrude","SWEPT_FACE",FACE,{"disambiguationData":[OSD([sQuery(id+"F1.wireOp",EDGE,"E8")])]}),makeQuery(id+"F18.opExtrude","SWEPT_FACE",FACE,{"disambiguationData":[OSD([sQuery(id+"F12.wireOp",EDGE,"E47")])]})]});
            var sketch = newSketch(context, id + "F36", { "sketchPlane" : qUnion([Q0])});
            skCircle(sketch, "E98", {"center": v(-66.04, 0) * mm, "radius": 6.73 * mm});
            skSolve(sketch);
        }
        {
            var Q0;
            Q0 = qSketchRegion(id + "F36", true);
            extrude(context, id + "F37", {"entities" : qUnion([Q0]), "operationType" : NewBodyOperationType.REMOVE, "oppositeDirection" : true, "depth" : 31.37 * mm, "offsetDistance" : 25.4 * mm});
        }
        {
            var Q0;
            Q0=makeQuery(id+"F18.boolean.opBoolean","MERGE",FACE,{"derivedFrom":[makeQuery(id+"F6.opExtrude","SWEPT_FACE",FACE,{"disambiguationData":[OSD([sQuery(id+"F1.wireOp",EDGE,"E8")])]}),makeQuery(id+"F18.opExtrude","SWEPT_FACE",FACE,{"disambiguationData":[OSD([sQuery(id+"F12.wireOp",EDGE,"E47")])]})]});
            var sketch = newSketch(context, id + "F38", { "sketchPlane" : qUnion([Q0])});
            skCircle(sketch, "E99", {"center": v(-66.04, 0) * mm, "radius": 7.11 * mm});
            skSolve(sketch);
        }
        {
            var Q0;
            Q0 = qSketchRegion(id + "F38", true);
            extrude(context, id + "F39", {"entities" : qUnion([Q0]), "operationType" : NewBodyOperationType.REMOVE, "oppositeDirection" : true, "depth" : 24.38 * mm, "offsetDistance" : 25.4 * mm});
        }
        {
            var Q0;
            Q0=makeQuery(id+"F6.opExtrude","SWEPT_FACE",FACE,{"disambiguationData":[OSD([sQuery(id+"F1.wireOp",EDGE,"E12")])]});
            var sketch = newSketch(context, id + "F40", { "sketchPlane" : qUnion([Q0])});
            skLineSegment(sketch, "E100", {"start": v(0, 3.18) * mm, "end": v(7.33, -9.53) * mm});
            skLineSegment(sketch, "E101", {"start": v(7.33, -9.53) * mm, "end": v(0, -9.53) * mm});
            skLineSegment(sketch, "E102", {"start": v(0, -9.53) * mm, "end": v(0, 3.17) * mm});
            skSolve(sketch);
        }
        {
            var Q0;
            Q0 = qSketchRegion(id + "F40", true);
            extrude(context, id + "F41", {"entities" : qUnion([Q0]), "operationType" : NewBodyOperationType.REMOVE, "endBound" : BoundingType.THROUGH_ALL, "oppositeDirection" : true, "depth" : 25.4 * mm, "offsetDistance" : 25.4 * mm});
        }
        {
            var Q0;
            Q0=makeQuery(id+"F18.opExtrude","SWEPT_FACE",FACE,{"disambiguationData":[OSD([sQuery(id+"F12.wireOp",EDGE,"E50")])]});
            var sketch = newSketch(context, id + "F42", { "sketchPlane" : qUnion([Q0])});
            skLineSegment(sketch, "E103", {"start": v(132.08, -3.17) * mm, "end": v(124.75, 9.53) * mm});
            skLineSegment(sketch, "E104", {"start": v(124.75, 9.53) * mm, "end": v(132.08, 9.53) * mm});
            skLineSegment(sketch, "E105", {"start": v(132.08, 9.53) * mm, "end": v(132.08, -3.18) * mm});
            skSolve(sketch);
        }
        {
            var Q0;
            Q0 = qSketchRegion(id + "F42", true);
            extrude(context, id + "F43", {"entities" : qUnion([Q0]), "operationType" : NewBodyOperationType.REMOVE, "endBound" : BoundingType.THROUGH_ALL, "oppositeDirection" : true, "depth" : 25.4 * mm, "offsetDistance" : 25.4 * mm});
        }
    });
